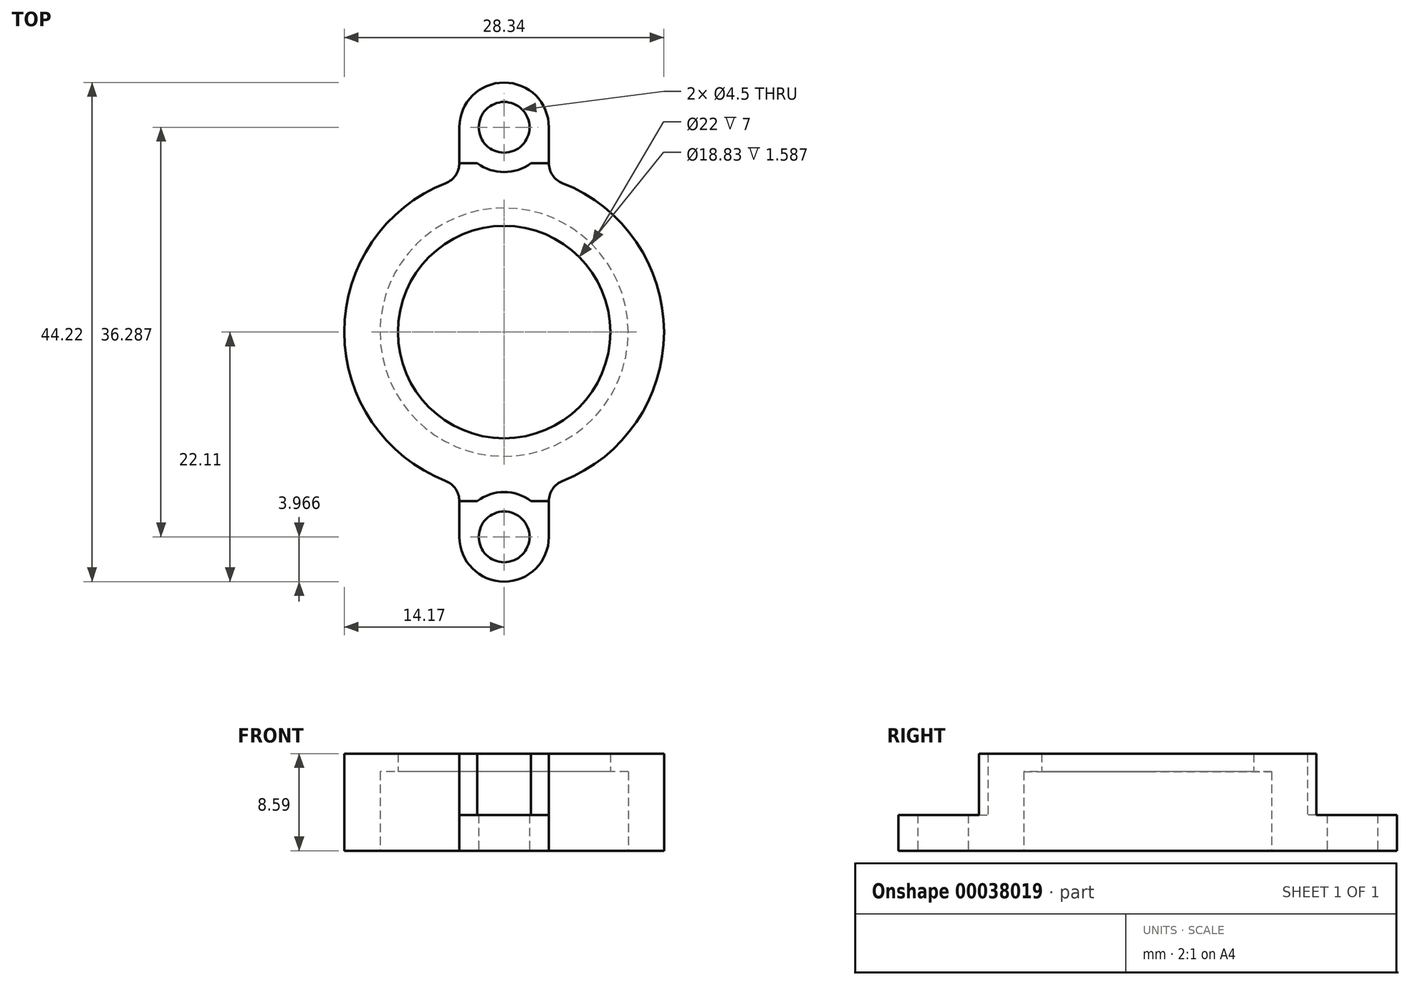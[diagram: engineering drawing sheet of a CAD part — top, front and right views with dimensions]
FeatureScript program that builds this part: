
annotation { "Feature Type Name" : "Feature", "Feature Type Description" : "" }
export const myFeature = defineFeature(function(context is Context, id is Id, definition is map)
    precondition{}
    {
        {
            var Q0;
            Q0=qCreatedBy(makeId("Top.planeOp"),FACE);
            var sketch = newSketch(context, id + "F0", { "sketchPlane" : qUnion([Q0])});
            skCircle(sketch, "E0", {"center": v(0, 0) * mm, "radius": 11 * mm});
            skLineSegment(sketch, "E1", {"start": v(0, 18.14) * mm, "end": v(0, -18.14) * mm, "construction": true});
            skArc(sketch, "E2", {"start": v(3.97, -13.6) * mm, "mid": v(14.17, 0) * mm, "end": v(3.97, 13.6) * mm});
            skArc(sketch, "E3", {"start": v(-3.97, 13.6) * mm, "mid": v(-14.17, 0) * mm, "end": v(-3.97, -13.6) * mm});
            skLineSegment(sketch, "E4", {"start": v(-3.97, 18.14) * mm, "end": v(3.97, 18.14) * mm, "construction": true});
            skLineSegment(sketch, "E5", {"start": v(-3.97, -18.14) * mm, "end": v(3.97, -18.14) * mm, "construction": true});
            skArc(sketch, "E6", {"start": v(3.97, 18.14) * mm, "mid": v(0, 22.11) * mm, "end": v(-3.97, 18.14) * mm});
            skArc(sketch, "E7", {"start": v(-3.97, -18.14) * mm, "mid": v(0, -22.11) * mm, "end": v(3.97, -18.14) * mm});
            skArc(sketch, "E8", {"start": v(-3.97, 18.14) * mm, "mid": v(0, 14.17) * mm, "end": v(3.97, 18.14) * mm, "construction": true});
            skLineSegment(sketch, "E9", {"start": v(3.97, -18.14) * mm, "end": v(3.97, -13.6) * mm});
            skLineSegment(sketch, "E10", {"start": v(-3.97, -18.14) * mm, "end": v(-3.97, -13.6) * mm});
            skLineSegment(sketch, "E11", {"start": v(3.97, 18.14) * mm, "end": v(3.97, 13.6) * mm});
            skLineSegment(sketch, "E12", {"start": v(-3.97, 18.14) * mm, "end": v(-3.97, 13.6) * mm});
            skCircle(sketch, "E13", {"center": v(0, 18.14) * mm, "radius": 2.25 * mm});
            skCircle(sketch, "E14", {"center": v(0, -18.14) * mm, "radius": 2.25 * mm});
            skArc(sketch, "E15", {"start": v(3.97, 13.6) * mm, "mid": v(0, 14.17) * mm, "end": v(-3.97, 13.6) * mm, "construction": true});
            skSolve(sketch);
        }
        {
            var Q0;
            Q0 = qSketchRegion(id + "F0", true);
            extrude(context, id + "F1", {"entities" : qUnion([Q0]), "depth" : 3.17 * mm});
        }
        {
            var Q0;
            Q0=makeQuery(id+"F1.opExtrude","CAP_FACE",FACE,{"disambiguationData":[OSD([sQuery(id+"F0.wireOp",EDGE,"E0"),sQuery(id+"F0.wireOp",EDGE,"E2"),sQuery(id+"F0.wireOp",EDGE,"E3"),sQuery(id+"F0.wireOp",EDGE,"E6"),sQuery(id+"F0.wireOp",EDGE,"E7"),sQuery(id+"F0.wireOp",EDGE,"E9"),sQuery(id+"F0.wireOp",EDGE,"E10"),sQuery(id+"F0.wireOp",EDGE,"E11"),sQuery(id+"F0.wireOp",EDGE,"E12"),sQuery(id+"F0.wireOp",EDGE,"E13"),sQuery(id+"F0.wireOp",EDGE,"E14")])],"isStart":false});
            var sketch = newSketch(context, id + "F2", { "sketchPlane" : qUnion([Q0])});
            skArc(sketch, "E16", {"start": v(-2.38, 14.97) * mm, "mid": v(0, 14.17) * mm, "end": v(2.38, 14.97) * mm});
            skLineSegment(sketch, "E17", {"start": v(-2.38, 14.97) * mm, "end": v(-3.97, 14.97) * mm});
            skLineSegment(sketch, "E18", {"start": v(2.38, 14.97) * mm, "end": v(3.97, 14.97) * mm});
            skLineSegment(sketch, "E19", {"start": v(3.97, 14.97) * mm, "end": v(3.97, 13.6) * mm});
            skLineSegment(sketch, "E20", {"start": v(-3.97, 14.97) * mm, "end": v(-3.97, 13.6) * mm});
            skArc(sketch, "E21", {"start": v(-3.97, 13.6) * mm, "mid": v(-14.17, 0) * mm, "end": v(-3.97, -13.6) * mm});
            skArc(sketch, "E22", {"start": v(3.97, -13.6) * mm, "mid": v(14.17, 0) * mm, "end": v(3.97, 13.6) * mm});
            skCircle(sketch, "E23", {"center": v(0, 0) * mm, "radius": 11 * mm});
            skLineSegment(sketch, "E24", {"start": v(-3.97, -13.6) * mm, "end": v(-3.97, -14.97) * mm});
            skLineSegment(sketch, "E25", {"start": v(3.97, -13.6) * mm, "end": v(3.97, -14.97) * mm});
            skLineSegment(sketch, "E26", {"start": v(3.97, -14.97) * mm, "end": v(2.38, -14.97) * mm});
            skLineSegment(sketch, "E27", {"start": v(-3.97, -14.97) * mm, "end": v(-2.38, -14.97) * mm});
            skArc(sketch, "E28", {"start": v(2.38, -14.97) * mm, "mid": v(0, -14.17) * mm, "end": v(-2.38, -14.97) * mm});
            skSolve(sketch);
        }
        {
            var Q0;
            Q0 = qSketchRegion(id + "F2", true);
            extrude(context, id + "F3", {"entities" : qUnion([Q0]), "operationType" : NewBodyOperationType.ADD, "depth" : 3.83 * mm});
        }
        {
            var Q0;
            Q0=makeQuery(id+"F3.opExtrude","CAP_FACE",FACE,{"disambiguationData":[OSD([sQuery(id+"F2.wireOp",EDGE,"E16"),sQuery(id+"F2.wireOp",EDGE,"E17"),sQuery(id+"F2.wireOp",EDGE,"E18"),sQuery(id+"F2.wireOp",EDGE,"E19"),sQuery(id+"F2.wireOp",EDGE,"E20"),sQuery(id+"F2.wireOp",EDGE,"E21"),sQuery(id+"F2.wireOp",EDGE,"E22"),sQuery(id+"F2.wireOp",EDGE,"E23"),sQuery(id+"F2.wireOp",EDGE,"E24"),sQuery(id+"F2.wireOp",EDGE,"E25"),sQuery(id+"F2.wireOp",EDGE,"E26"),sQuery(id+"F2.wireOp",EDGE,"E27"),sQuery(id+"F2.wireOp",EDGE,"E28")])],"isStart":false});
            var sketch = newSketch(context, id + "F4", { "sketchPlane" : qUnion([Q0])});
            skCircle(sketch, "E29", {"center": v(0, 0) * mm, "radius": 9.41 * mm});
            skSolve(sketch);
        }
        {
            var Q0;
            Q0=makeQuery(id+"F4.imprint","IMPRINT",FACE,{"disambiguationData":[TD([[makeQuery(id+"F4.imprint","IMPRINT",EDGE,{"derivedFrom":sQuery(id+"F4.wireOp",EDGE,"E29")}),-1.0]])]});
            var Q1;
            Q1=makeQuery(id+"F4.imprint","IMPRINT",FACE,{"disambiguationData":[TD([[makeQuery(id+"F4.imprint","IMPRINT",EDGE,{"derivedFrom":makeQuery(id+"F3.opExtrude","CAP_EDGE",EDGE,{"disambiguationData":[OSD([sQuery(id+"F2.wireOp",EDGE,"E16")])],"isStart":false})}),-1.0]])]});
            extrude(context, id + "F5", {"entities" : qUnion([Q0, Q1]), "operationType" : NewBodyOperationType.ADD, "depth" : 1.59 * mm});
        }
        {
            var Q0;
            Q0=makeQuery(id+"F5.opExtrude","CAP_FACE",FACE,{"disambiguationData":[OSD([sQuery(id+"F2.wireOp",EDGE,"E16"),sQuery(id+"F2.wireOp",EDGE,"E17"),sQuery(id+"F2.wireOp",EDGE,"E18"),sQuery(id+"F2.wireOp",EDGE,"E19"),sQuery(id+"F2.wireOp",EDGE,"E20"),sQuery(id+"F2.wireOp",EDGE,"E21"),sQuery(id+"F2.wireOp",EDGE,"E22"),sQuery(id+"F2.wireOp",EDGE,"E24"),sQuery(id+"F2.wireOp",EDGE,"E25"),sQuery(id+"F2.wireOp",EDGE,"E26"),sQuery(id+"F2.wireOp",EDGE,"E27"),sQuery(id+"F2.wireOp",EDGE,"E28"),sQuery(id+"F4.wireOp",EDGE,"E29")])],"isStart":false});
            var sketch = newSketch(context, id + "F6", { "sketchPlane" : qUnion([Q0])});
            skArc(sketch, "E30", {"start": v(-5.18, 13.2) * mm, "mid": v(-4.3, 13.9) * mm, "end": v(-3.97, 14.97) * mm});
            skArc(sketch, "E31", {"start": v(3.97, 14.97) * mm, "mid": v(4.3, 13.9) * mm, "end": v(5.18, 13.2) * mm});
            skArc(sketch, "E32", {"start": v(-3.97, -14.97) * mm, "mid": v(-4.3, -13.9) * mm, "end": v(-5.18, -13.2) * mm});
            skArc(sketch, "E33", {"start": v(5.18, -13.2) * mm, "mid": v(4.3, -13.9) * mm, "end": v(3.97, -14.97) * mm});
            skArc(sketch, "E34", {"start": v(-5.18, -13.2) * mm, "mid": v(-4.58, -13.42) * mm, "end": v(-3.97, -13.6) * mm});
            skArc(sketch, "E35", {"start": v(3.97, -13.6) * mm, "mid": v(4.58, -13.42) * mm, "end": v(5.18, -13.2) * mm});
            skArc(sketch, "E36", {"start": v(5.18, 13.2) * mm, "mid": v(4.58, 13.42) * mm, "end": v(3.97, 13.6) * mm});
            skArc(sketch, "E37", {"start": v(-3.97, 13.6) * mm, "mid": v(-4.58, 13.42) * mm, "end": v(-5.18, 13.2) * mm});
            skLineSegment(sketch, "E38", {"start": v(3.97, 14.97) * mm, "end": v(3.97, 13.6) * mm});
            skLineSegment(sketch, "E39", {"start": v(-3.97, 14.97) * mm, "end": v(-3.97, 13.6) * mm});
            skLineSegment(sketch, "E40", {"start": v(3.97, -13.6) * mm, "end": v(3.97, -14.97) * mm});
            skLineSegment(sketch, "E41", {"start": v(-3.97, -13.6) * mm, "end": v(-3.97, -14.97) * mm});
            skSolve(sketch);
        }
        {
            var Q0;
            Q0 = qSketchRegion(id + "F6", true);
            var Q1;
            Q1=makeQuery(id+"F1.opExtrude","CAP_FACE",FACE,{"disambiguationData":[OSD([sQuery(id+"F0.wireOp",EDGE,"E0"),sQuery(id+"F0.wireOp",EDGE,"E2"),sQuery(id+"F0.wireOp",EDGE,"E3"),sQuery(id+"F0.wireOp",EDGE,"E6"),sQuery(id+"F0.wireOp",EDGE,"E7"),sQuery(id+"F0.wireOp",EDGE,"E9"),sQuery(id+"F0.wireOp",EDGE,"E10"),sQuery(id+"F0.wireOp",EDGE,"E11"),sQuery(id+"F0.wireOp",EDGE,"E12"),sQuery(id+"F0.wireOp",EDGE,"E13"),sQuery(id+"F0.wireOp",EDGE,"E14")])],"isStart":true});
            extrude(context, id + "F7", {"entities" : qUnion([Q0]), "operationType" : NewBodyOperationType.ADD, "endBound" : BoundingType.UP_TO_SURFACE, "oppositeDirection" : true, "endBoundEntityFace" : qUnion([Q1]), "depth" : 25.4 * mm});
        }
    });
